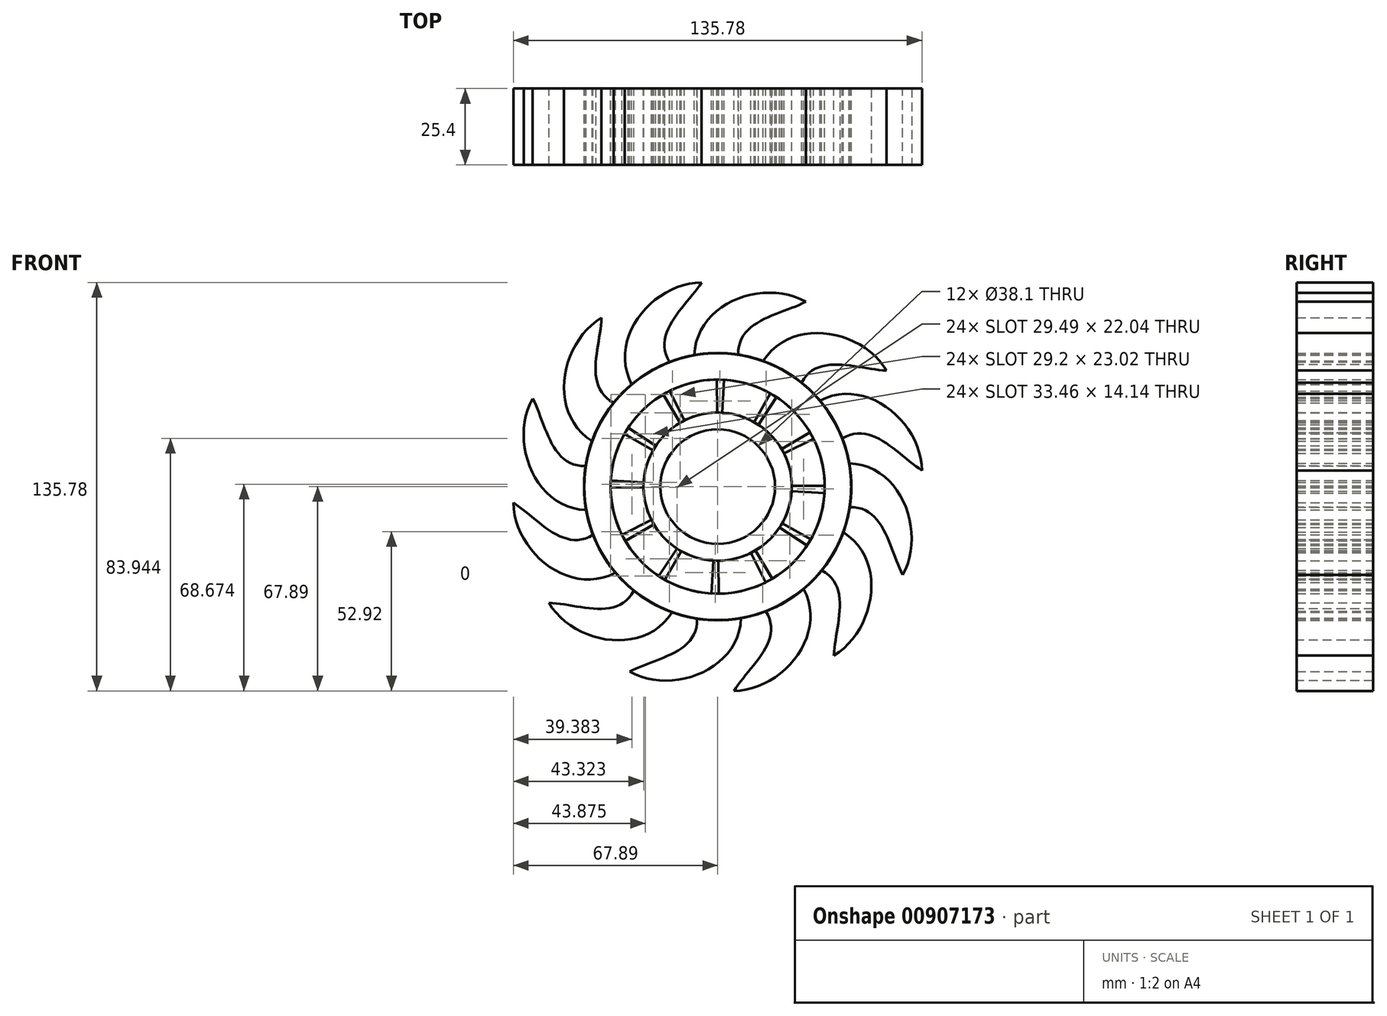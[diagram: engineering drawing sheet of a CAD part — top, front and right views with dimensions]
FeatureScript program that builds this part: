
annotation { "Feature Type Name" : "Feature", "Feature Type Description" : "" }
export const myFeature = defineFeature(function(context is Context, id is Id, definition is map)
    precondition{}
    {
        {
            var Q0;
            Q0=qCreatedBy(makeId("Front.planeOp"),FACE);
            var sketch = newSketch(context, id + "F0", { "sketchPlane" : qUnion([Q0])});
            skCircle(sketch, "E0", {"center": v(0, 0) * mm, "radius": 24.63 * mm});
            skCircle(sketch, "E1", {"center": v(0, 0) * mm, "radius": 35.59 * mm});
            skLineSegment(sketch, "E2", {"start": v(-30.98, 17.51) * mm, "end": v(-21.44, 12.12) * mm});
            skLineSegment(sketch, "E3", {"start": v(-29.72, 19.58) * mm, "end": v(-20.56, 13.55) * mm});
            skCircle(sketch, "E4", {"center": v(0, 0) * mm, "radius": 44.4 * mm});
            skLineSegment(sketch, "E5.1.0", {"start": v(-31.81, -15.95) * mm, "end": v(-22.02, -11.03) * mm});
            skLineSegment(sketch, "E5.1.1", {"start": v(-30.66, -18.07) * mm, "end": v(-21.21, -12.5) * mm});
            skLineSegment(sketch, "E5.2.0", {"start": v(-2.1, -35.52) * mm, "end": v(-1.45, -24.58) * mm});
            skLineSegment(sketch, "E5.2.1", {"start": v(0.32, -35.58) * mm, "end": v(0.22, -24.63) * mm});
            skLineSegment(sketch, "E5.3.0", {"start": v(29.72, -19.58) * mm, "end": v(20.56, -13.55) * mm});
            skLineSegment(sketch, "E5.3.1", {"start": v(30.98, -17.51) * mm, "end": v(21.44, -12.12) * mm});
            skLineSegment(sketch, "E5.4.0", {"start": v(31.81, 15.95) * mm, "end": v(22.02, 11.03) * mm});
            skLineSegment(sketch, "E5.4.1", {"start": v(30.66, 18.07) * mm, "end": v(21.21, 12.5) * mm});
            skLineSegment(sketch, "E5.5.0", {"start": v(2.1, 35.52) * mm, "end": v(1.45, 24.58) * mm});
            skLineSegment(sketch, "E5.5.1", {"start": v(-0.32, 35.58) * mm, "end": v(-0.22, 24.63) * mm});
            skFitSpline(sketch, "E6", {"points": [v(-41.74, 15.13) * mm, v(-38.6, 56.1) * mm], "startDerivative": vector(-44.75, 28.33) * mm, "endDerivative": vector(40.83, 24.16) * mm});
            skFitSpline(sketch, "E7", {"points": [v(-38.6, 56.1) * mm, v(-34.57, 27.86) * mm], "startDerivative": vector(-0.83, -27.5) * mm, "endDerivative": vector(30.86, -16.4) * mm});
            skCircle(sketch, "E8", {"center": v(0, 0) * mm, "radius": 19.05 * mm});
            skSolve(sketch);
        }
        {
            var Q0;
            Q0 = qSketchRegion(id + "F0", true);
            var Q1;
            {var subQ0=sQuery(id+"F0.wireOp",EDGE,"E5.3.0");Q1=makeQuery(id+"F0.imprint","IMPRINT",FACE,{"disambiguationData":[TD([[makeQuery(id+"F0.imprint","IMPRINT",EDGE,{"derivedFrom":subQ0}),-1.0]])]});}
            var Q2;
            {var subQ0=sQuery(id+"F0.wireOp",EDGE,"E5.4.0");Q2=makeQuery(id+"F0.imprint","IMPRINT",FACE,{"disambiguationData":[TD([[makeQuery(id+"F0.imprint","IMPRINT",EDGE,{"derivedFrom":subQ0}),-1.0]])]});}
            var Q3;
            {var subQ0=sQuery(id+"F0.wireOp",EDGE,"E5.5.0");Q3=makeQuery(id+"F0.imprint","IMPRINT",FACE,{"disambiguationData":[TD([[makeQuery(id+"F0.imprint","IMPRINT",EDGE,{"derivedFrom":subQ0}),-1.0]])]});}
            var Q4;
            {var subQ0=sQuery(id+"F0.wireOp",EDGE,"E2");Q4=makeQuery(id+"F0.imprint","IMPRINT",FACE,{"disambiguationData":[TD([[makeQuery(id+"F0.imprint","IMPRINT",EDGE,{"derivedFrom":subQ0}),1.0]])]});}
            var Q5;
            {var subQ0=sQuery(id+"F0.wireOp",EDGE,"E5.1.0");Q5=makeQuery(id+"F0.imprint","IMPRINT",FACE,{"disambiguationData":[TD([[makeQuery(id+"F0.imprint","IMPRINT",EDGE,{"derivedFrom":subQ0}),-1.0]])]});}
            var Q6;
            {var subQ0=sQuery(id+"F0.wireOp",EDGE,"E5.2.0");Q6=makeQuery(id+"F0.imprint","IMPRINT",FACE,{"disambiguationData":[TD([[makeQuery(id+"F0.imprint","IMPRINT",EDGE,{"derivedFrom":subQ0}),-1.0]])]});}
            var Q7;
            Q7=makeQuery(id+"F0.imprint","IMPRINT",FACE,{"disambiguationData":[TD([[makeQuery(id+"F0.imprint","IMPRINT",EDGE,{"derivedFrom":sQuery(id+"F0.wireOp",EDGE,"E8")}),-1.0]])]});
            extrude(context, id + "F1", {"entities" : qUnion([Q0, Q1, Q2, Q3, Q4, Q5, Q6, Q7]), "depth" : 25.4 * mm, "offsetDistance" : 25.4 * mm});
        }
        {
            var Q0;
            Q0=qCreatedBy(makeId("Right.planeOp"),FACE);
            var sketch = newSketch(context, id + "F2", { "sketchPlane" : qUnion([Q0])});
            skLineSegment(sketch, "E9", {"start": v(0, 0) * mm, "end": v(-14.25, 0) * mm});
            skSolve(sketch);
        }
        {
            var Q0;
            Q0=makeQuery(id+"F1.opExtrude","SWEPT_BODY",BODY,{"disambiguationData":[OSD([sQuery(id+"F0.wireOp",EDGE,"E0"),sQuery(id+"F0.wireOp",EDGE,"E1"),sQuery(id+"F0.wireOp",EDGE,"E2"),sQuery(id+"F0.wireOp",EDGE,"E3"),sQuery(id+"F0.wireOp",EDGE,"E4"),sQuery(id+"F0.wireOp",EDGE,"E5.1.0"),sQuery(id+"F0.wireOp",EDGE,"E5.1.1"),sQuery(id+"F0.wireOp",EDGE,"E5.2.0"),sQuery(id+"F0.wireOp",EDGE,"E5.2.1"),sQuery(id+"F0.wireOp",EDGE,"E5.3.0"),sQuery(id+"F0.wireOp",EDGE,"E5.3.1"),sQuery(id+"F0.wireOp",EDGE,"E5.4.0"),sQuery(id+"F0.wireOp",EDGE,"E5.4.1"),sQuery(id+"F0.wireOp",EDGE,"E5.5.0"),sQuery(id+"F0.wireOp",EDGE,"E5.5.1"),sQuery(id+"F0.wireOp",EDGE,"E6"),sQuery(id+"F0.wireOp",EDGE,"E7"),sQuery(id+"F0.wireOp",EDGE,"E8")])]});
            var Q1;
            Q1=sQuery(id+"F2.wireOp",EDGE,"E9");
            circularPattern(context, id + "F3", {"entities" : qUnion([Q0]), "axis" : qUnion([Q1]), "angle" : 360 * degree, "instanceCount" : 12, "equalSpace" : true});
        }
    });
